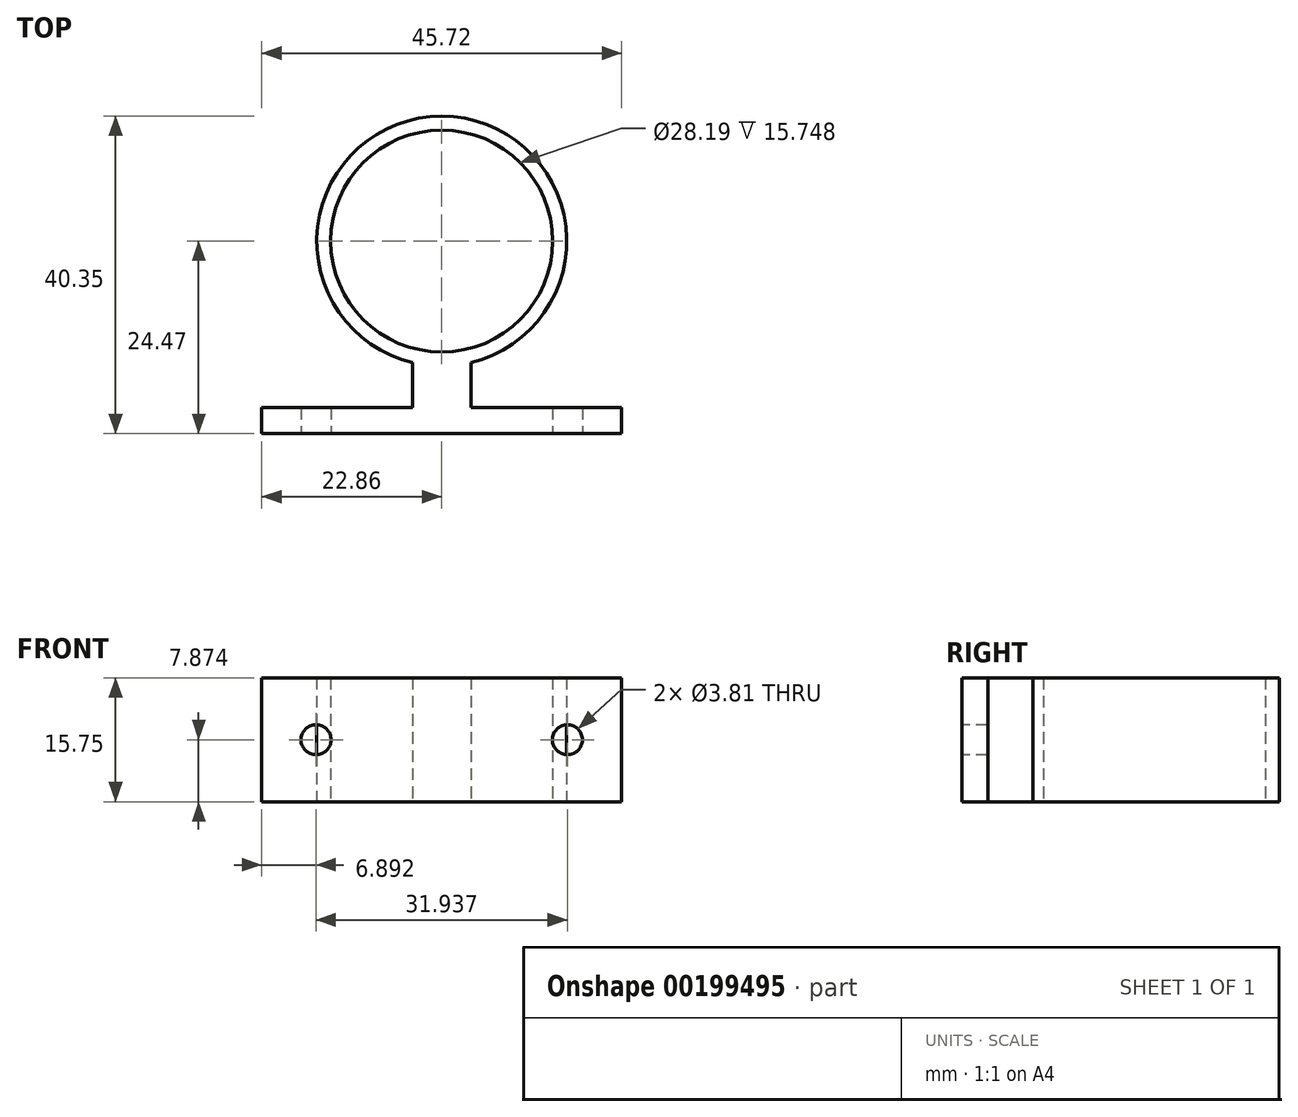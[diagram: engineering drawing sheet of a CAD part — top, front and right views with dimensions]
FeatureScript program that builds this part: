
annotation { "Feature Type Name" : "Feature", "Feature Type Description" : "" }
export const myFeature = defineFeature(function(context is Context, id is Id, definition is map)
    precondition{}
    {
        {
            var Q0;
            Q0=qCreatedBy(makeId("Top.planeOp"),FACE);
            var sketch = newSketch(context, id + "F0", { "sketchPlane" : qUnion([Q0])});
            skCircle(sketch, "E0", {"center": v(0, 0) * mm, "radius": 14.1 * mm});
            skCircle(sketch, "E1", {"center": v(0, 0) * mm, "radius": 15.88 * mm});
            skLineSegment(sketch, "E2.bottom", {"start": v(-3.7, -15.2) * mm, "end": v(3.7, -15.2) * mm});
            skLineSegment(sketch, "E2.top", {"start": v(-3.7, -22.81) * mm, "end": v(3.7, -22.81) * mm});
            skLineSegment(sketch, "E2.left", {"start": v(-3.7, -15.2) * mm, "end": v(-3.7, -22.81) * mm});
            skLineSegment(sketch, "E2.right", {"start": v(3.7, -15.2) * mm, "end": v(3.7, -22.81) * mm});
            skPoint(sketch, "E2.middle", {"position": v(0, -19) * mm});
            skLineSegment(sketch, "E3.bottom", {"start": v(22.86, -21.16) * mm, "end": v(-22.86, -21.16) * mm});
            skLineSegment(sketch, "E3.top", {"start": v(22.86, -24.47) * mm, "end": v(-22.86, -24.47) * mm});
            skLineSegment(sketch, "E3.left", {"start": v(22.86, -21.16) * mm, "end": v(22.86, -24.47) * mm});
            skLineSegment(sketch, "E3.right", {"start": v(-22.86, -21.16) * mm, "end": v(-22.86, -24.47) * mm});
            skPoint(sketch, "E3.middle", {"position": v(0, -22.81) * mm});
            skSolve(sketch);
        }
        {
            var Q0;
            Q0 = qSketchRegion(id + "F0", true);
            extrude(context, id + "F1", {"entities" : qUnion([Q0]), "depth" : 15.75 * mm});
        }
        {
            var Q0;
            Q0=makeQuery(id+"F1.opExtrude","SWEPT_FACE",FACE,{"disambiguationData":[OSD([sQuery(id+"F0.wireOp",EDGE,"E3.top")])]});
            var sketch = newSketch(context, id + "F2", { "sketchPlane" : qUnion([Q0])});
            skCircle(sketch, "E4", {"center": v(-15.97, 7.87) * mm, "radius": 1.9 * mm});
            skPoint(sketch, "E4.centerSnap0", {"position": v(-22.86, 7.87) * mm});
            skLineSegment(sketch, "E5", {"start": v(0, 15.75) * mm, "end": v(0, 0) * mm});
            skCircle(sketch, "E6.MirrorC", {"center": v(15.97, 7.87) * mm, "radius": 1.9 * mm});
            skSolve(sketch);
        }
        {
            var Q0;
            Q0 = qSketchRegion(id + "F2", true);
            extrude(context, id + "F3", {"entities" : qUnion([Q0]), "operationType" : NewBodyOperationType.REMOVE, "oppositeDirection" : true, "depth" : 9.47 * mm});
        }
    });
